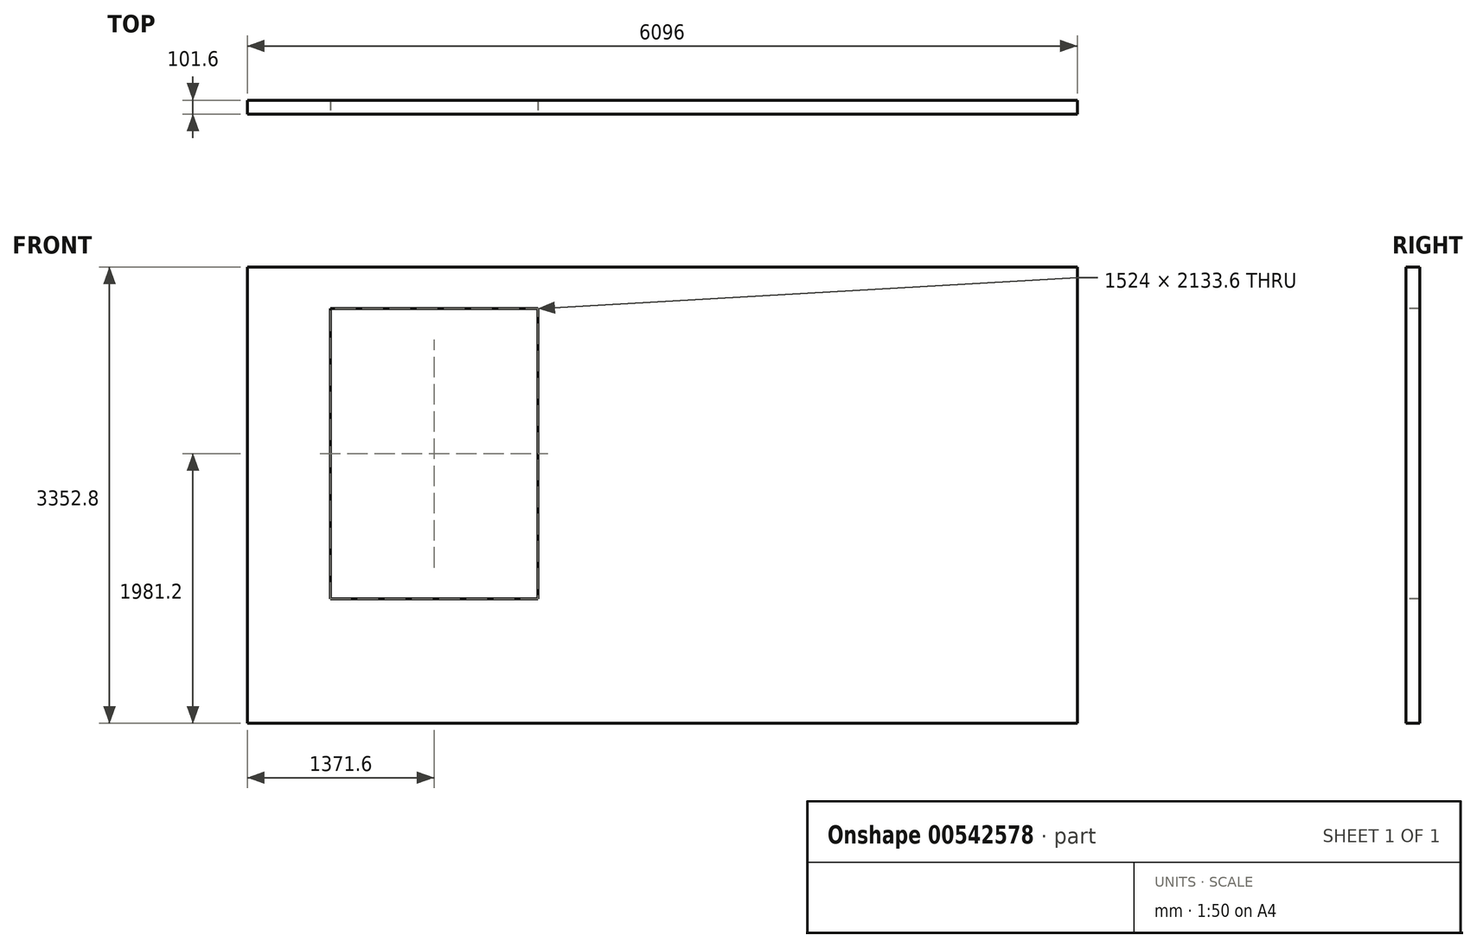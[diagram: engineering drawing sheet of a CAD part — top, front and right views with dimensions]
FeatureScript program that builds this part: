
annotation { "Feature Type Name" : "Feature", "Feature Type Description" : "" }
export const myFeature = defineFeature(function(context is Context, id is Id, definition is map)
    precondition{}
    {
        {
            var Q0;
            Q0=qCreatedBy(makeId("Front.planeOp"),FACE);
            var sketch = newSketch(context, id + "F0", { "sketchPlane" : qUnion([Q0])});
            skLineSegment(sketch, "E0.bottom", {"start": v(0, 0) * mm, "end": v(-6096, 0) * mm});
            skLineSegment(sketch, "E0.top", {"start": v(0, 3352.8) * mm, "end": v(-6096, 3352.8) * mm});
            skLineSegment(sketch, "E0.left", {"start": v(0, 0) * mm, "end": v(0, 3352.8) * mm});
            skLineSegment(sketch, "E0.right", {"start": v(-6096, 0) * mm, "end": v(-6096, 3352.8) * mm});
            skSolve(sketch);
        }
        {
            var Q0;
            Q0=makeQuery(id+"F0.imprint","IMPRINT",FACE,{"disambiguationData":[TD([[makeQuery(id+"F0.imprint","IMPRINT",EDGE,{"derivedFrom":sQuery(id+"F0.wireOp",EDGE,"E0.bottom")}),-1.0]])]});
            extrude(context, id + "F1", {"entities" : qUnion([Q0]), "depth" : 101.6 * mm, "offsetDistance" : 30.48 * mm});
        }
        {
            var Q0;
            Q0=makeQuery(id+"F1.opExtrude","CAP_FACE",FACE,{"disambiguationData":[OSD([sQuery(id+"F0.wireOp",EDGE,"E0.bottom"),sQuery(id+"F0.wireOp",EDGE,"E0.top"),sQuery(id+"F0.wireOp",EDGE,"E0.left"),sQuery(id+"F0.wireOp",EDGE,"E0.right")])],"isStart":false});
            var sketch = newSketch(context, id + "F2", { "sketchPlane" : qUnion([Q0])});
            skLineSegment(sketch, "E1.bottom", {"start": v(-6096, 0) * mm, "end": v(-5486.4, 0) * mm, "construction": true});
            skLineSegment(sketch, "E1.top", {"start": v(-6096, 914.4) * mm, "end": v(-5486.4, 914.4) * mm, "construction": true});
            skLineSegment(sketch, "E1.left", {"start": v(-6096, 0) * mm, "end": v(-6096, 914.4) * mm, "construction": true});
            skLineSegment(sketch, "E1.right", {"start": v(-5486.4, 0) * mm, "end": v(-5486.4, 914.4) * mm, "construction": true});
            skLineSegment(sketch, "E2.bottom", {"start": v(-5486.4, 914.4) * mm, "end": v(-3962.4, 914.4) * mm});
            skLineSegment(sketch, "E2.top", {"start": v(-5486.4, 3048) * mm, "end": v(-3962.4, 3048) * mm});
            skLineSegment(sketch, "E2.left", {"start": v(-5486.4, 914.4) * mm, "end": v(-5486.4, 3048) * mm});
            skLineSegment(sketch, "E2.right", {"start": v(-3962.4, 914.4) * mm, "end": v(-3962.4, 3048) * mm});
            skSolve(sketch);
        }
        {
            var Q0;
            Q0=makeQuery(id+"F2.imprint","IMPRINT",FACE,{"disambiguationData":[TD([[makeQuery(id+"F2.imprint","IMPRINT",EDGE,{"derivedFrom":sQuery(id+"F2.wireOp",EDGE,"E2.bottom")}),1.0]])]});
            extrude(context, id + "F3", {"entities" : qUnion([Q0]), "operationType" : NewBodyOperationType.REMOVE, "oppositeDirection" : true, "depth" : 188.98 * mm, "offsetDistance" : 30.48 * mm});
        }
    });
